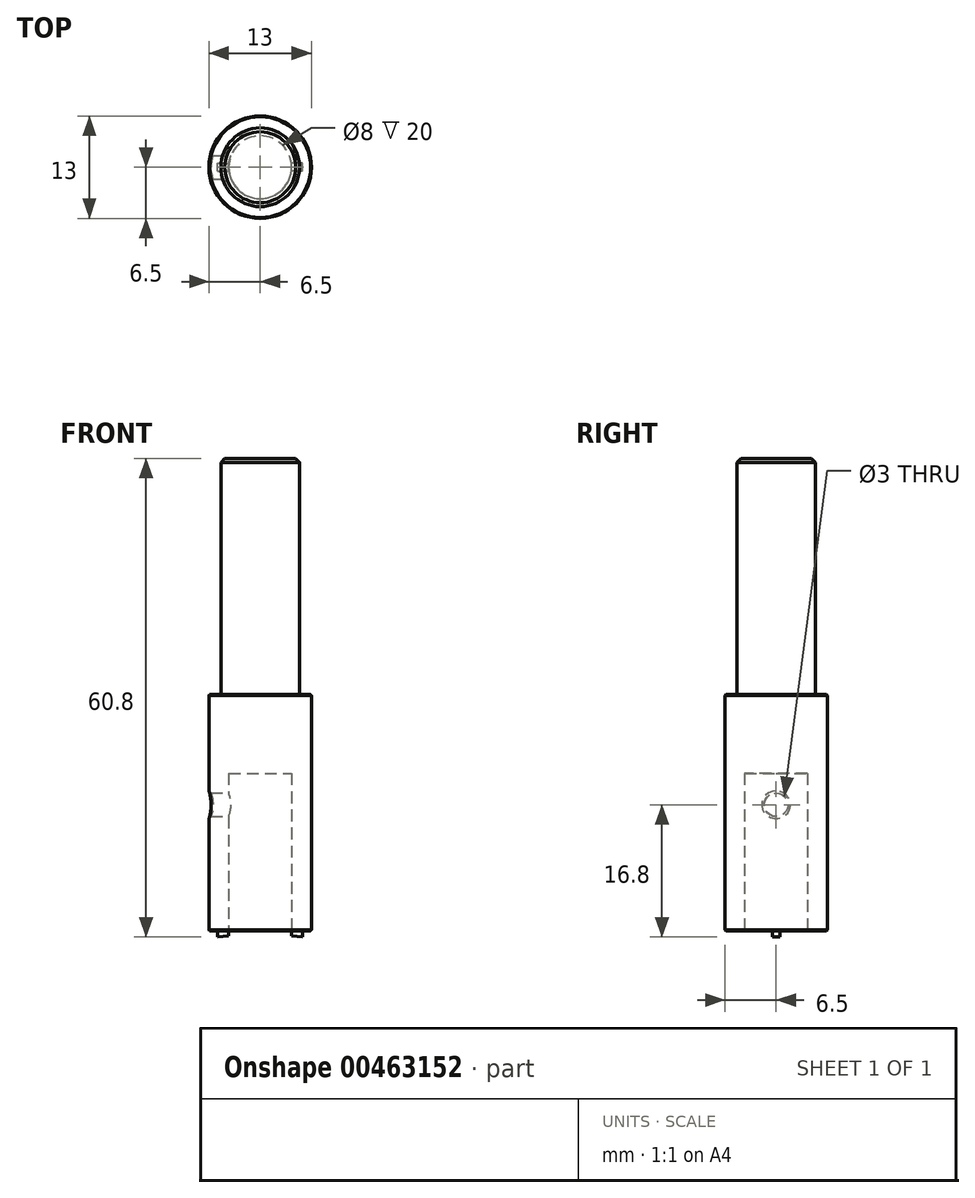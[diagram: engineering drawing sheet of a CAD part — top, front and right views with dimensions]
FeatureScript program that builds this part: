
annotation { "Feature Type Name" : "Feature", "Feature Type Description" : "" }
export const myFeature = defineFeature(function(context is Context, id is Id, definition is map)
    precondition{}
    {
        {
            var Q0;
            Q0=qCreatedBy(makeId("Top.planeOp"),FACE);
            var sketch = newSketch(context, id + "F0", { "sketchPlane" : qUnion([Q0])});
            skCircle(sketch, "E0", {"center": v(0, 0) * mm, "radius": 6.5 * mm});
            skSolve(sketch);
        }
        {
            var Q0;
            Q0 = qSketchRegion(id + "F0", true);
            var Q1;
            Q1=makeQuery(id+"F0.imprint","IMPRINT",FACE,{"disambiguationData":[TD([[makeQuery(id+"F0.imprint","IMPRINT",EDGE,{"derivedFrom":sQuery(id+"F0.wireOp",EDGE,"E0")}),1.0]])]});
            extrude(context, id + "F1", {"entities" : qUnion([Q0, Q1]), "depth" : 30 * mm});
        }
        {
            var Q0;
            Q0=makeQuery(id+"F1.opExtrude","CAP_FACE",FACE,{"disambiguationData":[OSD([sQuery(id+"F0.wireOp",EDGE,"E0")])],"isStart":false});
            var sketch = newSketch(context, id + "F2", { "sketchPlane" : qUnion([Q0])});
            skCircle(sketch, "E1", {"center": v(0, 0) * mm, "radius": 5 * mm});
            skSolve(sketch);
        }
        {
            var Q0;
            Q0=makeQuery(id+"F2.imprint","IMPRINT",FACE,{"disambiguationData":[TD([[makeQuery(id+"F2.imprint","IMPRINT",EDGE,{"derivedFrom":sQuery(id+"F2.wireOp",EDGE,"E1")}),1.0]])]});
            extrude(context, id + "F3", {"entities" : qUnion([Q0]), "operationType" : NewBodyOperationType.ADD, "depth" : 30 * mm});
        }
        {
            var Q0;
            Q0=makeQuery(id+"F1.opExtrude","CAP_FACE",FACE,{"disambiguationData":[OSD([sQuery(id+"F0.wireOp",EDGE,"E0")])],"isStart":true});
            var sketch = newSketch(context, id + "F4", { "sketchPlane" : qUnion([Q0])});
            skCircle(sketch, "E2", {"center": v(0, 0) * mm, "radius": 4 * mm});
            skSolve(sketch);
        }
        {
            var Q0;
            Q0 = qSketchRegion(id + "F4", true);
            extrude(context, id + "F5", {"entities" : qUnion([Q0]), "operationType" : NewBodyOperationType.REMOVE, "oppositeDirection" : true, "depth" : 20 * mm});
        }
        {
            var Q0;
            Q0=qCreatedBy(makeId("Right.planeOp"),FACE);
            var sketch = newSketch(context, id + "F6", { "sketchPlane" : qUnion([Q0])});
            skCircle(sketch, "E3", {"center": v(0, 16) * mm, "radius": 1.5 * mm});
            skSolve(sketch);
        }
        {
            var Q0;
            Q0 = qSketchRegion(id + "F6", true);
            extrude(context, id + "F7", {"entities" : qUnion([Q0]), "operationType" : NewBodyOperationType.REMOVE, "oppositeDirection" : true, "depth" : 25 * mm});
        }
        {
            var Q0;
            Q0=makeQuery(id+"F1.opExtrude","CAP_EDGE",EDGE,{"disambiguationData":[OSD([sQuery(id+"F0.wireOp",EDGE,"E0")])],"isStart":true});
            var Q1;
            Q1=makeQuery(id+"F1.opExtrude","CAP_EDGE",EDGE,{"disambiguationData":[OSD([sQuery(id+"F0.wireOp",EDGE,"E0")])],"isStart":false});
            chamfer(context, id + "F8", {"entities" : qUnion([Q0, Q1]), "width" : .1 * mm, "tangentPropagation" : true});
        }
        {
            var Q0;
            Q0=makeQuery(id+"F3.opExtrude","CAP_EDGE",EDGE,{"disambiguationData":[OSD([sQuery(id+"F2.wireOp",EDGE,"E1")])],"isStart":false});
            chamfer(context, id + "F9", {"entities" : qUnion([Q0]), "width" : .5 * mm, "tangentPropagation" : true});
        }
        {
            var Q0;
            Q0=makeQuery(id+"F7.boolean.opBoolean","INTERSECT",EDGE,{"derivedFrom":[makeQuery(id+"F1.opExtrude","SWEPT_FACE",FACE,{"disambiguationData":[OSD([sQuery(id+"F0.wireOp",EDGE,"E0")])]}),makeQuery(id+"F7.opExtrude","SWEPT_FACE",FACE,{"disambiguationData":[OSD([sQuery(id+"F6.wireOp",EDGE,"E3")])]})]});
            chamfer(context, id + "F10", {"entities" : qUnion([Q0]), "width" : .25 * mm, "tangentPropagation" : true});
        }
        {
            var Q0;
            Q0=qCreatedBy(makeId("Front.planeOp"),FACE);
            var sketch = newSketch(context, id + "F11", { "sketchPlane" : qUnion([Q0])});
            skPoint(sketch, "E4", {"position": v(-5.4, 0) * mm});
            skPoint(sketch, "E5", {"position": v(-4, 0) * mm});
            skLineSegment(sketch, "E6", {"start": v(-5.4, 0) * mm, "end": v(-5.4, -0.8) * mm});
            skLineSegment(sketch, "E7", {"start": v(-5.4, -0.8) * mm, "end": v(-4, -0.68) * mm});
            skLineSegment(sketch, "E8", {"start": v(-4, 0) * mm, "end": v(-4, -0.68) * mm});
            skLineSegment(sketch, "E9", {"start": v(-5.4, 0) * mm, "end": v(-4, 0) * mm});
            skLineSegment(sketch, "E10.MirrorCS", {"start": v(5.4, -0.8) * mm, "end": v(4, -0.68) * mm});
            skLineSegment(sketch, "E11.MirrorCS", {"start": v(5.4, 0) * mm, "end": v(4, 0) * mm});
            skPoint(sketch, "E12.MirrorP", {"position": v(4, 0) * mm});
            skPoint(sketch, "E13.MirrorP", {"position": v(5.4, 0) * mm});
            skLineSegment(sketch, "E14.MirrorCS", {"start": v(4, 0) * mm, "end": v(4, -0.68) * mm});
            skLineSegment(sketch, "E15.MirrorCS", {"start": v(5.4, 0) * mm, "end": v(5.4, -0.8) * mm});
            skSolve(sketch);
        }
        {
            var Q0;
            Q0 = qSketchRegion(id + "F11", true);
            extrude(context, id + "F12", {"entities" : qUnion([Q0]), "operationType" : NewBodyOperationType.ADD, "depth" : 1 * mm, "offsetDistance" : 25 * mm, "symmetric" : true});
        }
    });
